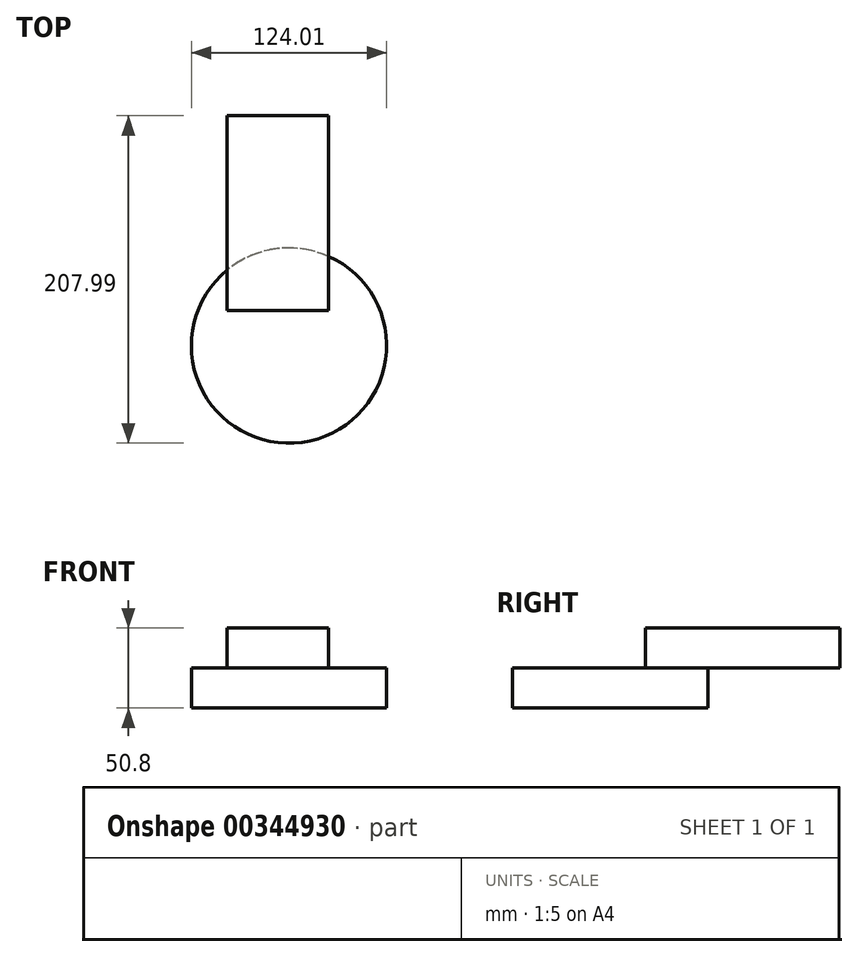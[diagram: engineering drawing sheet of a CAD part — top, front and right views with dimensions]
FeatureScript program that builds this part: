
annotation { "Feature Type Name" : "Feature", "Feature Type Description" : "" }
export const myFeature = defineFeature(function(context is Context, id is Id, definition is map)
    precondition{}
    {
        {
            var Q0;
            Q0=qCreatedBy(makeId("Top.planeOp"),FACE);
            var sketch = newSketch(context, id + "F0", { "sketchPlane" : qUnion([Q0])});
            skCircle(sketch, "E0", {"center": v(39.37, -22.28) * mm, "radius": 62 * mm});
            skSolve(sketch);
        }
        {
            var Q0;
            Q0 = qSketchRegion(id + "F0", true);
            extrude(context, id + "F1", {"entities" : qUnion([Q0]), "depth" : 25.4 * mm});
        }
        {
            var Q0;
            Q0=makeQuery(id+"F1.opExtrude","CAP_FACE",FACE,{"disambiguationData":[OSD([sQuery(id+"F0.wireOp",EDGE,"E0")])],"isStart":false});
            var sketch = newSketch(context, id + "F2", { "sketchPlane" : qUnion([Q0])});
            skLineSegment(sketch, "E1.bottom", {"start": v(0, 0) * mm, "end": v(64.6, 0) * mm});
            skLineSegment(sketch, "E1.top", {"start": v(0, 123.71) * mm, "end": v(64.6, 123.71) * mm});
            skLineSegment(sketch, "E1.left", {"start": v(0, 0) * mm, "end": v(0, 123.71) * mm});
            skLineSegment(sketch, "E1.right", {"start": v(64.6, 0) * mm, "end": v(64.6, 123.71) * mm});
            skPoint(sketch, "E1.middle", {"position": v(32.3, 61.86) * mm});
            skSolve(sketch);
        }
        {
            var Q0;
            Q0 = qSketchRegion(id + "F2", true);
            var Q1;
            {var subQ0=sQuery(id+"F2.wireOp",EDGE,"E1.top");Q1=makeQuery(id+"F2.imprint","IMPRINT",FACE,{"disambiguationData":[TD([[makeQuery(id+"F2.imprint","IMPRINT",EDGE,{"derivedFrom":subQ0}),-1.0]])]});}
            extrude(context, id + "F3", {"entities" : qUnion([Q0, Q1]), "operationType" : NewBodyOperationType.ADD, "depth" : 25.4 * mm});
        }
    });
